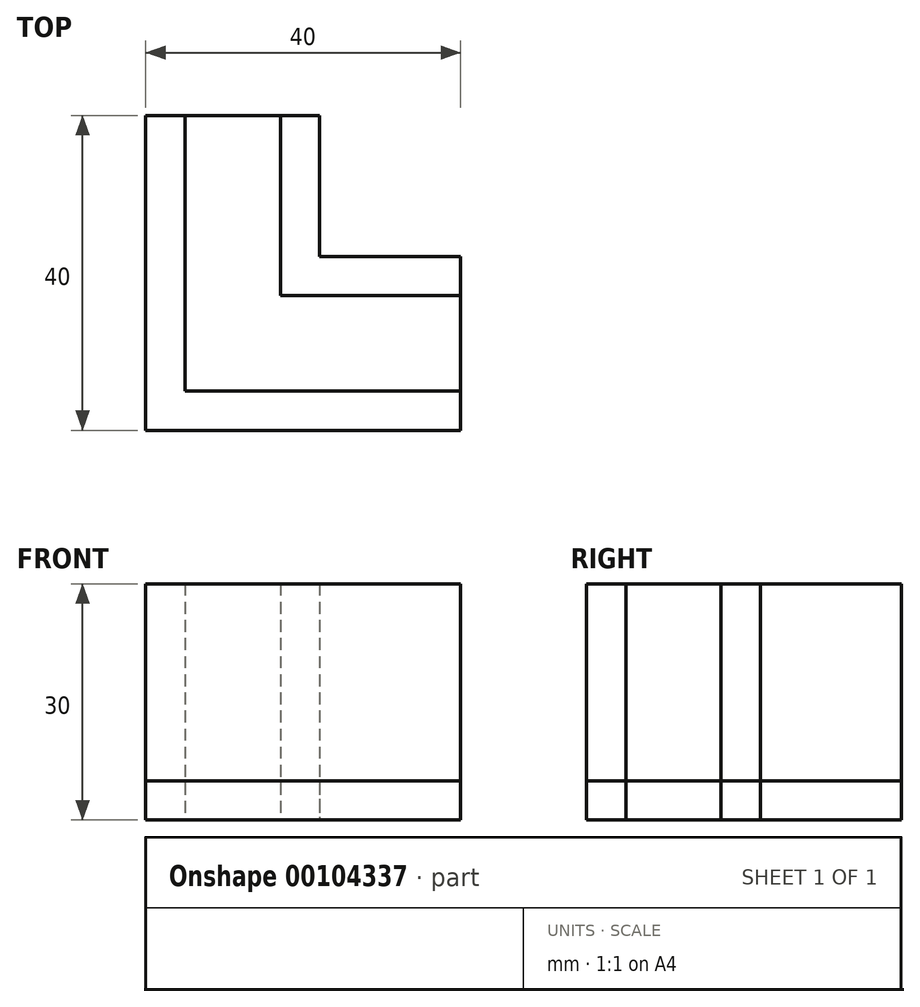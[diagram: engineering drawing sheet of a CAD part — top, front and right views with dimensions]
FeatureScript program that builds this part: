
annotation { "Feature Type Name" : "Feature", "Feature Type Description" : "" }
export const myFeature = defineFeature(function(context is Context, id is Id, definition is map)
    precondition{}
    {
        {
            var Q0;
            Q0=qCreatedBy(makeId("Top.planeOp"),FACE);
            var sketch = newSketch(context, id + "F0", { "sketchPlane" : qUnion([Q0])});
            skLineSegment(sketch, "E0", {"start": v(0, 0) * mm, "end": v(35, 0) * mm});
            skLineSegment(sketch, "E1", {"start": v(35, 0) * mm, "end": v(35, 12.1) * mm});
            skLineSegment(sketch, "E2", {"start": v(35, 12.1) * mm, "end": v(12.1, 12.1) * mm});
            skLineSegment(sketch, "E3", {"start": v(12.1, 12.1) * mm, "end": v(12.1, 35) * mm});
            skLineSegment(sketch, "E4", {"start": v(12.1, 35) * mm, "end": v(0, 35) * mm});
            skLineSegment(sketch, "E5", {"start": v(0, 35) * mm, "end": v(0, 0) * mm});
            skLineSegment(sketch, "E6", {"start": v(0, 35) * mm, "end": v(-5, 35) * mm});
            skLineSegment(sketch, "E7", {"start": v(-5, 35) * mm, "end": v(-5, -5) * mm});
            skLineSegment(sketch, "E8", {"start": v(-5, -5) * mm, "end": v(35, -5) * mm});
            skLineSegment(sketch, "E9", {"start": v(35, -5) * mm, "end": v(35, 0) * mm});
            skLineSegment(sketch, "E10", {"start": v(12.1, 35) * mm, "end": v(17.1, 35) * mm});
            skLineSegment(sketch, "E11", {"start": v(17.1, 35) * mm, "end": v(17.1, 17.1) * mm});
            skLineSegment(sketch, "E12", {"start": v(17.1, 17.1) * mm, "end": v(35, 17.1) * mm});
            skLineSegment(sketch, "E13", {"start": v(35, 17.1) * mm, "end": v(35, 12.1) * mm});
            skSolve(sketch);
        }
        {
            var Q0;
            Q0=makeQuery(id+"F0.imprint","IMPRINT",FACE,{"disambiguationData":[TD([[makeQuery(id+"F0.imprint","IMPRINT",EDGE,{"derivedFrom":sQuery(id+"F0.wireOp",EDGE,"E0")}),-1.0]])]});
            var Q1;
            Q1=makeQuery(id+"F0.imprint","IMPRINT",FACE,{"disambiguationData":[TD([[makeQuery(id+"F0.imprint","IMPRINT",EDGE,{"derivedFrom":sQuery(id+"F0.wireOp",EDGE,"E2")}),-1.0]])]});
            extrude(context, id + "F1", {"entities" : qUnion([Q0, Q1]), "depth" : 30 * mm});
        }
        {
            var Q0;
            Q0 = qSketchRegion(id + "F0", true);
            extrude(context, id + "F2", {"entities" : qUnion([Q0]), "depth" : 5 * mm});
        }
    });
